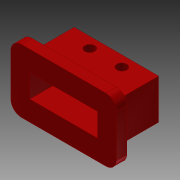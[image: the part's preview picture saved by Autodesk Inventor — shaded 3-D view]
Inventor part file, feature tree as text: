
AUTODESK INVENTOR PART (.ipt)
format: ipt  version: 2015 (Build 190159000, 159)  size: 122,880 bytes
history: native  units: in
note: dims shown in document units (in); Inventor stores cm internally (conversion verified against a paired STEP export)
features: extrude x3, sketch x3, shell x1
ambient origin geometry x8: Origin, YZ Plane, XZ Plane, XY Plane, X Axis, Y Axis, Z Axis, Center Point
bodies: Solid1 (feature_tree)
feature tree (7):
  extrude  "Extrusion1"  Depth=0.474in
  shell  "Shell1"  Thickness=0.5in
  extrude  "Extrusion2"  Depth=0.125in
  extrude  "Extrusion3"  Depth=0.125in
  sketch  "Sketch1"  dims[d0=1.0in d1=0.474in d2=0.5in d3=0.0in]
  sketch  "Sketch2"  dims[d4=0.1in d23=0.125in]
  sketch  "Sketch3"  dims[d24=0.12in d25=0.38in d26=0.5in d27=0.0in d28=0.75in d29=1.25in d30=0.125in d31=0.125in d32=0.0in]
